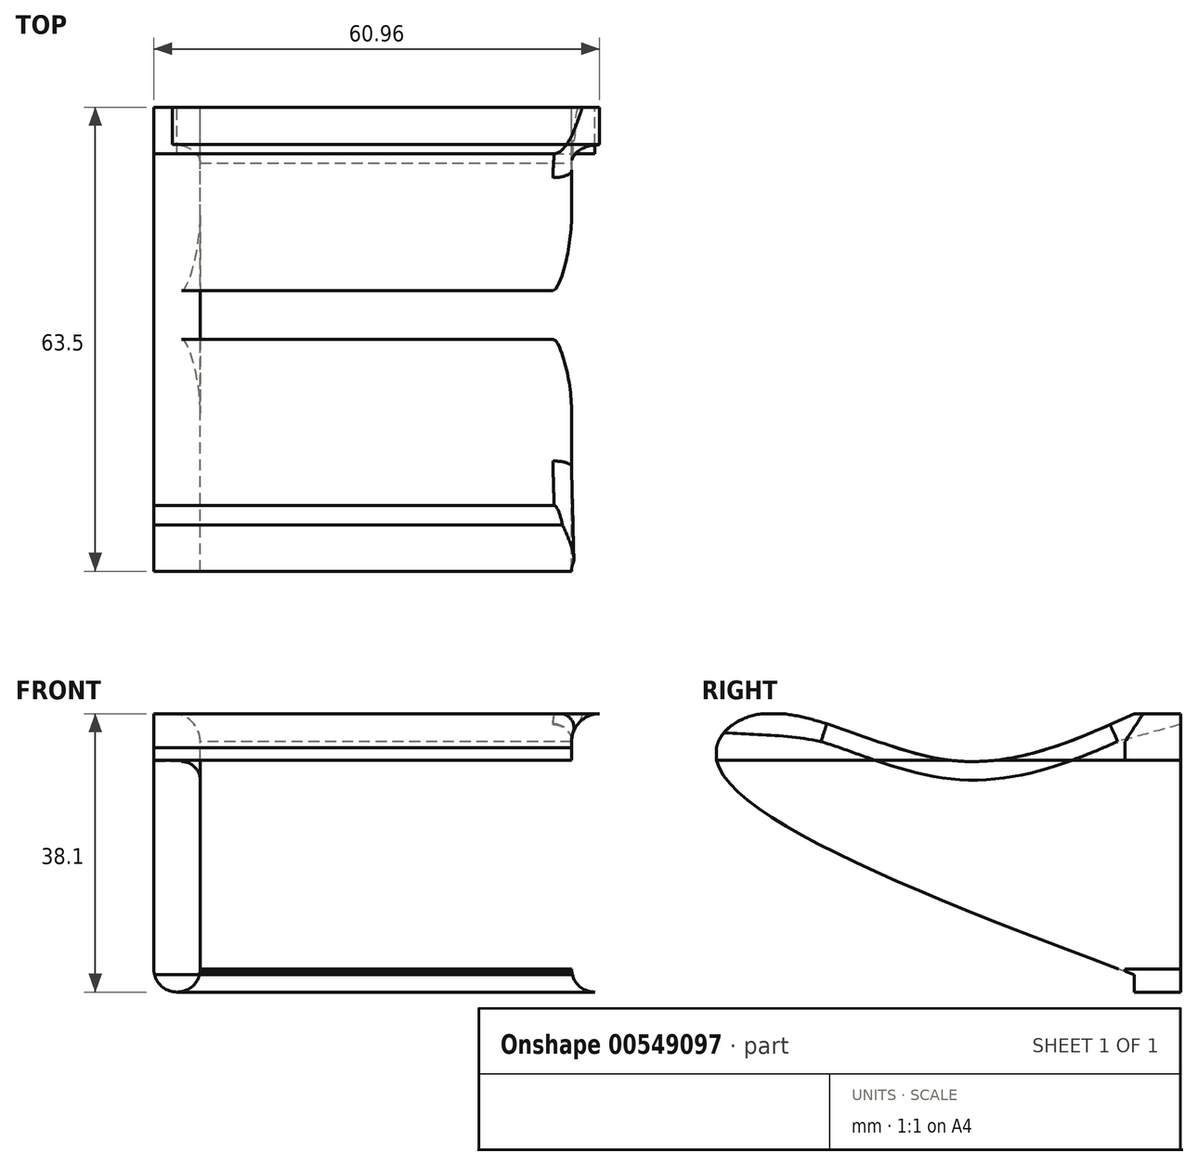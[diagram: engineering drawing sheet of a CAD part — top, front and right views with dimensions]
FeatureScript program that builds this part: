
annotation { "Feature Type Name" : "Feature", "Feature Type Description" : "" }
export const myFeature = defineFeature(function(context is Context, id is Id, definition is map)
    precondition{}
    {
        {
            var Q0;
            Q0=qCreatedBy(makeId("Front.planeOp"),FACE);
            var sketch = newSketch(context, id + "F0", { "sketchPlane" : qUnion([Q0])});
            skLineSegment(sketch, "E0.bottom", {"start": v(25.4, -19.05) * mm, "end": v(-25.4, -19.05) * mm});
            skLineSegment(sketch, "E0.top", {"start": v(25.4, 19.05) * mm, "end": v(-25.4, 19.05) * mm});
            skLineSegment(sketch, "E0.left", {"start": v(25.4, -15.88) * mm, "end": v(25.4, 15.24) * mm});
            skLineSegment(sketch, "E0.right", {"start": v(-25.4, -15.88) * mm, "end": v(-25.4, 15.24) * mm});
            skPoint(sketch, "E0.middle", {"position": v(0, 0) * mm});
            skLineSegment(sketch, "E1", {"start": v(-29.21, 19.05) * mm, "end": v(-31.75, 19.05) * mm});
            skLineSegment(sketch, "E2", {"start": v(-31.75, 19.05) * mm, "end": v(-31.75, -15.88) * mm});
            skLineSegment(sketch, "E3", {"start": v(-28.58, -19.05) * mm, "end": v(-28.58, -19.05) * mm});
            skLineSegment(sketch, "E4", {"start": v(0, -19.05) * mm, "end": v(0, 19.05) * mm, "construction": true});
            skPoint(sketch, "E5.visualSharp", {"position": v(-25.4, 19.05) * mm});
            skArc(sketch, "E5.filletArc", {"start": v(-25.4, 15.24) * mm, "mid": v(-26.52, 17.93) * mm, "end": v(-29.21, 19.05) * mm});
            skPoint(sketch, "E6.visualSharp", {"position": v(-25.4, -19.05) * mm});
            skArc(sketch, "E6.filletArc", {"start": v(-28.58, -19.05) * mm, "mid": v(-26.33, -18.12) * mm, "end": v(-25.4, -15.88) * mm});
            skPoint(sketch, "E7.visualSharp", {"position": v(-31.75, -19.05) * mm});
            skArc(sketch, "E7.filletArc", {"start": v(-31.75, -15.88) * mm, "mid": v(-30.82, -18.12) * mm, "end": v(-28.58, -19.05) * mm});
            skLineSegment(sketch, "E8", {"start": v(-25.4, 19.05) * mm, "end": v(-31.75, 19.05) * mm});
            skLineSegment(sketch, "E9", {"start": v(-28.58, -19.05) * mm, "end": v(-25.4, -19.05) * mm});
            skArc(sketch, "E10.MirrorCS", {"start": v(25.4, 15.24) * mm, "mid": v(26.52, 17.93) * mm, "end": v(29.21, 19.05) * mm});
            skArc(sketch, "E11.MirrorCS", {"start": v(28.58, -19.05) * mm, "mid": v(26.33, -18.12) * mm, "end": v(25.4, -15.88) * mm});
            skArc(sketch, "E12.MirrorCS", {"start": v(31.75, -15.88) * mm, "mid": v(30.82, -18.12) * mm, "end": v(28.58, -19.05) * mm});
            skLineSegment(sketch, "E13.MirrorCS", {"start": v(31.75, 19.05) * mm, "end": v(31.75, -15.88) * mm});
            skLineSegment(sketch, "E14.MirrorCS", {"start": v(25.4, 19.05) * mm, "end": v(31.75, 19.05) * mm});
            skLineSegment(sketch, "E15.MirrorCS", {"start": v(28.58, -19.05) * mm, "end": v(25.4, -19.05) * mm});
            skLineSegment(sketch, "E16.bottom", {"start": v(-31.75, 19.05) * mm, "end": v(31.75, 19.05) * mm});
            skLineSegment(sketch, "E16.top", {"start": v(-25.4, 12.7) * mm, "end": v(25.4, 12.7) * mm});
            skLineSegment(sketch, "E16.left", {"start": v(-31.75, 19.05) * mm, "end": v(-31.75, 12.7) * mm});
            skLineSegment(sketch, "E16.right", {"start": v(31.75, 19.05) * mm, "end": v(31.75, 12.7) * mm});
            skLineSegment(sketch, "E17.bottom", {"start": v(-28.58, -19.05) * mm, "end": v(28.58, -19.05) * mm});
            skLineSegment(sketch, "E17.top", {"start": v(-25.4, -15.88) * mm, "end": v(25.4, -15.88) * mm});
            skLineSegment(sketch, "E18", {"start": v(28.58, -19.05) * mm, "end": v(29.21, 19.05) * mm, "construction": true});
            skSolve(sketch);
        }
        {
            var Q0;
            Q0=makeQuery(id+"F0.imprint","IMPRINT",FACE,{"disambiguationData":[TD([[makeQuery(id+"F0.imprint","IMPRINT",EDGE,{"derivedFrom":sQuery(id+"F0.wireOp",EDGE,"E2")}),1.0]])]});
            var Q1;
            {var subQ2=sQuery(id+"F0.wireOp",EDGE,"E10.MirrorCS");Q1=makeQuery(id+"F0.imprint","IMPRINT",FACE,{"disambiguationData":[TD([[makeQuery(id+"F0.imprint","IMPRINT",EDGE,{"derivedFrom":subQ2}),-1.0]])]});}
            extrude(context, id + "F1", {"entities" : qUnion([Q0, Q1]), "depth" : 63.5 * mm, "offsetDistance" : 25.4 * mm});
        }
        {
            var Q0;
            {var subQ3=sQuery(id+"F0.wireOp",EDGE,"E5.filletArc");Q0=makeQuery(id+"F0.imprint","IMPRINT",FACE,{"disambiguationData":[TD([[makeQuery(id+"F0.imprint","IMPRINT",EDGE,{"derivedFrom":subQ3}),-1.0]])]});}
            var Q1;
            {var subQ0=sQuery(id+"F0.wireOp",EDGE,"E6.filletArc");Q1=makeQuery(id+"F0.imprint","IMPRINT",FACE,{"disambiguationData":[TD([[makeQuery(id+"F0.imprint","IMPRINT",EDGE,{"derivedFrom":subQ0}),-1.0]])]});}
            extrude(context, id + "F2", {"entities" : qUnion([Q0, Q1]), "depth" : 7.62 * mm, "offsetDistance" : 25.4 * mm});
        }
        {
            var Q0;
            Q0=qCreatedBy(makeId("Right.planeOp"),FACE);
            var sketch = newSketch(context, id + "F3", { "sketchPlane" : qUnion([Q0])});
            skLineSegment(sketch, "E19", {"start": v(0, 19.05) * mm, "end": v(0, -19.05) * mm});
            skLineSegment(sketch, "E20", {"start": v(0, 19.05) * mm, "end": v(-63.5, 19.05) * mm});
            skLineSegment(sketch, "E21", {"start": v(0, -19.05) * mm, "end": v(-63.5, -19.05) * mm});
            skLineSegment(sketch, "E22", {"start": v(-63.5, -19.05) * mm, "end": v(-63.5, 19.05) * mm});
            skLineSegment(sketch, "E23", {"start": v(0, 19.05) * mm, "end": v(-6.35, 19.05) * mm, "construction": true});
            skLineSegment(sketch, "E24", {"start": v(0, 19.05) * mm, "end": v(0, 12.7) * mm, "construction": true});
            skLineSegment(sketch, "E25", {"start": v(-63.5, 19.05) * mm, "end": v(-57.15, 19.05) * mm, "construction": true});
            skLineSegment(sketch, "E26", {"start": v(-63.5, 19.05) * mm, "end": v(-63.5, 12.7) * mm, "construction": true});
            skPoint(sketch, "E27.1.internal.snap0", {"position": v(-31.75, 19.05) * mm});
            skFitSpline(sketch, "E27", {"points": [v(-6.35, 19.05) * mm, v(-31.75, 12.7) * mm, v(-57.15, 19.05) * mm, v(-63.5, 12.7) * mm, v(0, -19.05) * mm], "startDerivative": vector(-104.5, -47.48) * mm, "endDerivative": vector(237.73, -88.59) * mm});
            skLineSegment(sketch, "E28", {"start": v(-6.35, -19.05) * mm, "end": v(-6.35, -16.68) * mm});
            skSolve(sketch);
        }
        {
            var Q0;
            {var subQ0=sQuery(id+"F3.wireOp",EDGE,"E27");var subQ1=sQuery(id+"F3.wireOp",EDGE,"E20");var subQ2=makeQuery(id+"F3.imprint","INTERSECT",VERTEX,{"disambiguationData":[OD(0.0)],"derivedFrom":[subQ1,subQ0]});Q0=makeQuery(id+"F3.imprint","IMPRINT",FACE,{"disambiguationData":[TD([[makeQuery(id+"F3.imprint","IMPRINT",EDGE,{"disambiguationData":[TD([[subQ2,-1.0]])],"derivedFrom":subQ1}),1.0]])]});}
            var Q1;
            {var subQ0=sQuery(id+"F3.wireOp",EDGE,"E22");var subQ1=sQuery(id+"F3.wireOp",EDGE,"E20");var subQ2=makeQuery(id+"F3.imprint","INTERSECT",VERTEX,{"derivedFrom":[subQ1,subQ0]});Q1=makeQuery(id+"F3.imprint","IMPRINT",FACE,{"disambiguationData":[TD([[makeQuery(id+"F3.imprint","IMPRINT",EDGE,{"disambiguationData":[TD([[subQ2,1.0]])],"derivedFrom":subQ1}),1.0]])]});}
            var Q2;
            {var subQ3=sQuery(id+"F3.wireOp",EDGE,"E28");Q2=makeQuery(id+"F3.imprint","IMPRINT",FACE,{"disambiguationData":[TD([[makeQuery(id+"F3.imprint","IMPRINT",EDGE,{"derivedFrom":subQ3}),1.0]])]});}
            extrude(context, id + "F4", {"entities" : qUnion([Q0, Q1, Q2]), "operationType" : NewBodyOperationType.REMOVE, "endBound" : BoundingType.THROUGH_ALL, "oppositeDirection" : true, "depth" : 25.4 * mm, "offsetDistance" : 25.4 * mm, "hasSecondDirection" : true, "secondDirectionBound" : SecondDirectionBoundingType.THROUGH_ALL, "secondDirectionOppositeDirection" : false, "secondDirectionDepth" : 25.4 * mm});
        }
        {
            var Q0;
            {var subQ0=sQuery(id+"F3.wireOp",EDGE,"E27");var subQ1=sQuery(id+"F3.wireOp",EDGE,"E20");Q0=makeQuery(id+"F4.boolean.opBoolean","INTERSECT",EDGE,{"derivedFrom":[makeQuery(id+"F1.opExtrude","SWEPT_FACE",FACE,{"disambiguationData":[OSD([sQuery(id+"F0.wireOp",EDGE,"E0.right")])]}),makeQuery(id+"F4.opExtrude","SWEPT_FACE",FACE,{"disambiguationData":[OSD([subQ0]),TDD([makeQuery(id+"F3.imprint","IMPRINT",EDGE,{"disambiguationData":[TD([[makeQuery(id+"F3.imprint","INTERSECT",VERTEX,{"disambiguationData":[OD(0.0)],"derivedFrom":[subQ1,subQ0]}),-1.0]])],"derivedFrom":subQ0})])]})]});}
            var Q1;
            {var subQ0=sQuery(id+"F3.wireOp",EDGE,"E27");var subQ1=sQuery(id+"F3.wireOp",EDGE,"E20");Q1=makeQuery(id+"F4.boolean.opBoolean","INTERSECT",EDGE,{"derivedFrom":[makeQuery(id+"F1.opExtrude","SWEPT_FACE",FACE,{"disambiguationData":[OSD([sQuery(id+"F0.wireOp",EDGE,"E0.left")])]}),makeQuery(id+"F4.opExtrude","SWEPT_FACE",FACE,{"disambiguationData":[OSD([subQ0]),TDD([makeQuery(id+"F3.imprint","IMPRINT",EDGE,{"disambiguationData":[TD([[makeQuery(id+"F3.imprint","INTERSECT",VERTEX,{"disambiguationData":[OD(0.0)],"derivedFrom":[subQ1,subQ0]}),-1.0]])],"derivedFrom":subQ0})])]})]});}
            fillet(context, id + "F5", {"entities" : qUnion([Q0, Q1]), "radius" : 2.54 * mm, "tangentPropagation" : true, "allowEdgeOverflow" : false});
        }
        {
            var Q0;
            {var subQ0=sQuery(id+"F3.wireOp",EDGE,"E27");var subQ1=sQuery(id+"F3.wireOp",EDGE,"E20");Q0=makeQuery(id+"F4.boolean.opBoolean","INTERSECT",EDGE,{"derivedFrom":[makeQuery(id+"F2.opExtrude","CAP_FACE",FACE,{"disambiguationData":[OSD([sQuery(id+"F0.wireOp",EDGE,"E0.right"),sQuery(id+"F0.wireOp",EDGE,"E5.filletArc"),sQuery(id+"F0.wireOp",EDGE,"E10.MirrorCS"),sQuery(id+"F0.wireOp",EDGE,"E0.left"),sQuery(id+"F0.wireOp",EDGE,"E16.bottom"),sQuery(id+"F0.wireOp",EDGE,"E16.top")])],"isStart":false}),makeQuery(id+"F4.opExtrude","SWEPT_FACE",FACE,{"disambiguationData":[OSD([subQ0]),TDD([makeQuery(id+"F3.imprint","IMPRINT",EDGE,{"disambiguationData":[TD([[makeQuery(id+"F3.imprint","INTERSECT",VERTEX,{"disambiguationData":[OD(0.0)],"derivedFrom":[subQ1,subQ0]}),-1.0]])],"derivedFrom":subQ0})])]})]});}
            chamfer(context, id + "F6", {"entities" : qUnion([Q0]), "width" : 5.08 * mm, "tangentPropagation" : true});
        }
    });
